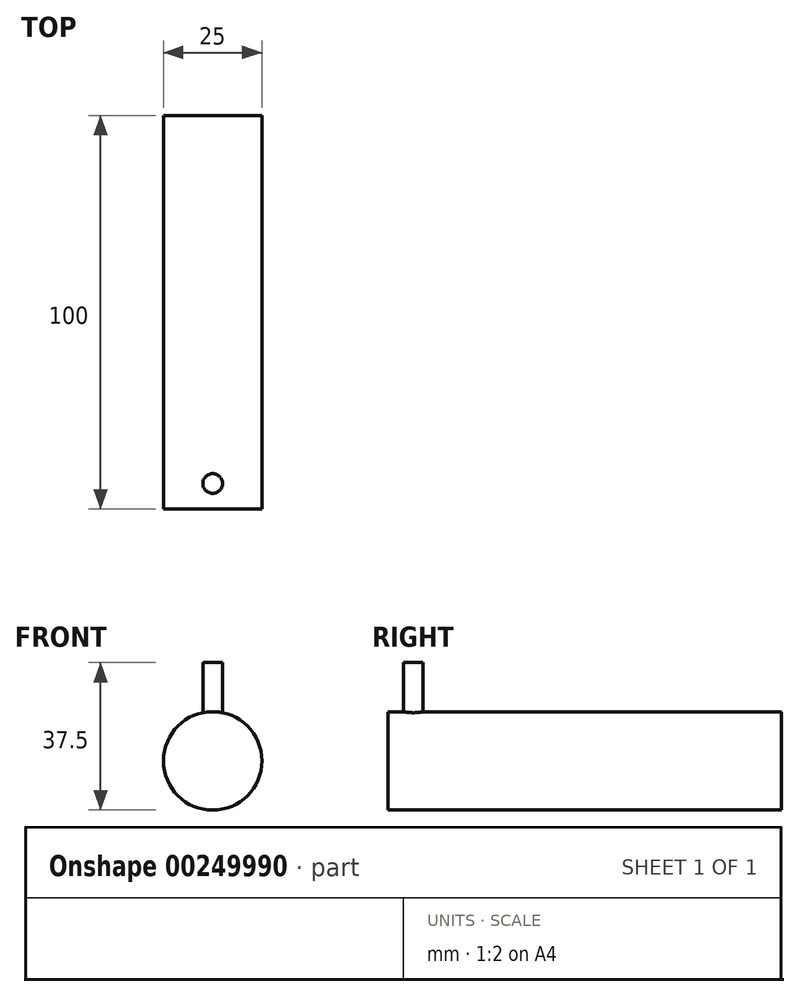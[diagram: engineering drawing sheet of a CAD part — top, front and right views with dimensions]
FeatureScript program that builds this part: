
annotation { "Feature Type Name" : "Feature", "Feature Type Description" : "" }
export const myFeature = defineFeature(function(context is Context, id is Id, definition is map)
    precondition{}
    {
        {
            var Q0;
            Q0=qCreatedBy(makeId("Front.planeOp"),FACE);
            var sketch = newSketch(context, id + "F0", { "sketchPlane" : qUnion([Q0])});
            skCircle(sketch, "E0", {"center": v(0, 0) * mm, "radius": 12.5 * mm});
            skSolve(sketch);
        }
        {
            var Q0;
            Q0 = qSketchRegion(id + "F0", true);
            extrude(context, id + "F1", {"entities" : qUnion([Q0]), "depth" : 100 * mm});
        }
        {
            var Q0;
            Q0=qCreatedBy(makeId("Top.planeOp"),FACE);
            var sketch = newSketch(context, id + "F2", { "sketchPlane" : qUnion([Q0])});
            skCircle(sketch, "E1", {"center": v(0, -93.53) * mm, "radius": 2.5 * mm});
            skSolve(sketch);
        }
        {
            var Q0;
            Q0 = qSketchRegion(id + "F2", true);
            extrude(context, id + "F3", {"entities" : qUnion([Q0]), "operationType" : NewBodyOperationType.ADD, "depth" : 25 * mm});
        }
    });
